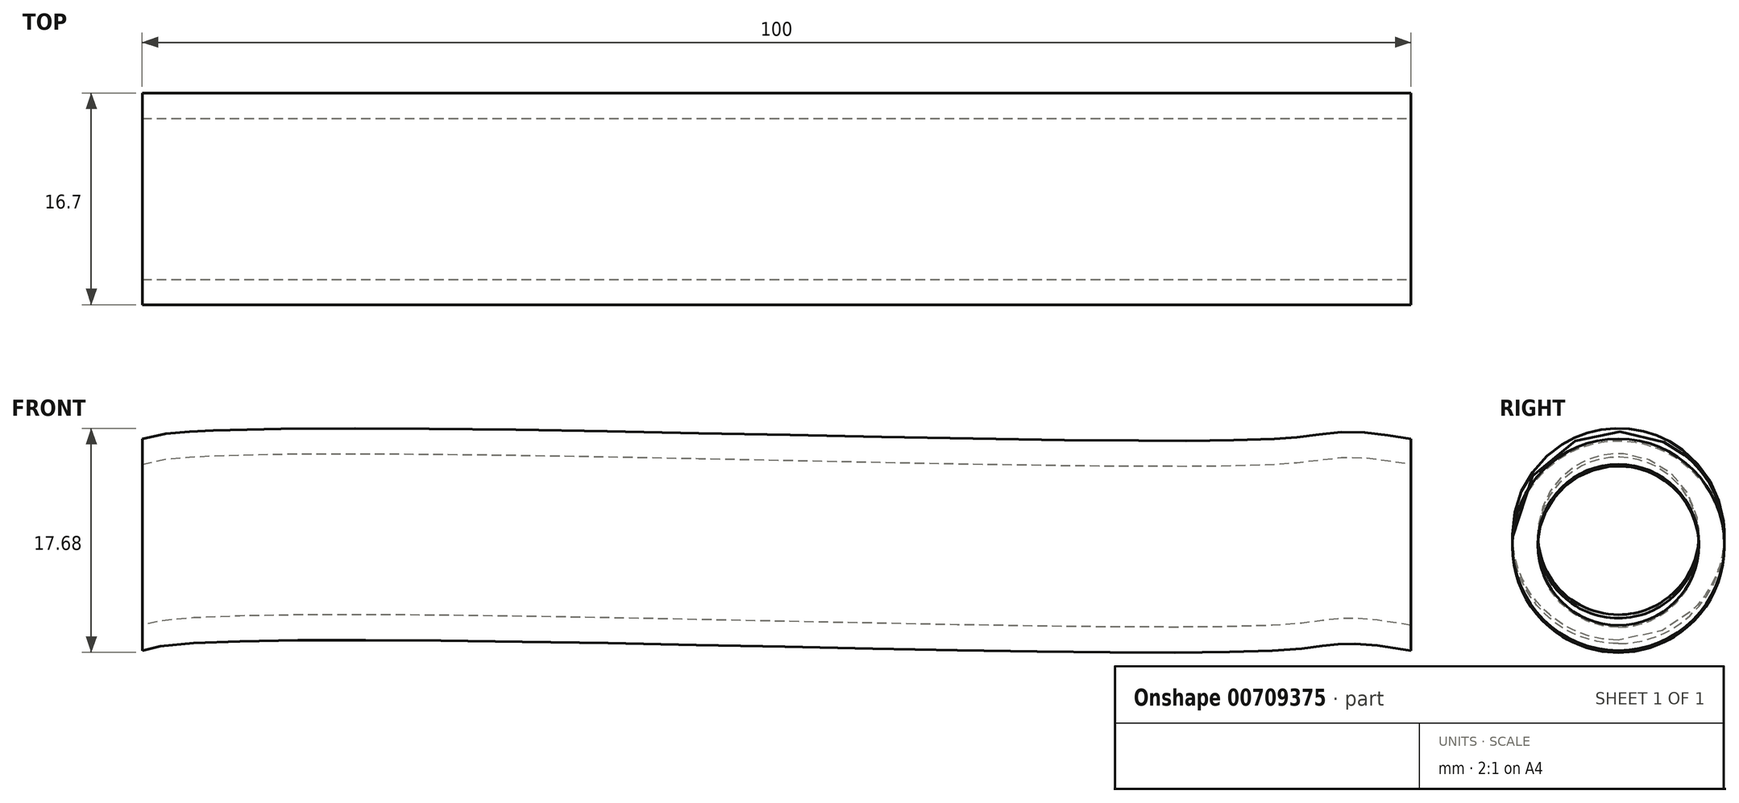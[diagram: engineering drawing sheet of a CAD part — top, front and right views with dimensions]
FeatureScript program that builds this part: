
annotation { "Feature Type Name" : "Feature", "Feature Type Description" : "" }
export const myFeature = defineFeature(function(context is Context, id is Id, definition is map)
    precondition{}
    {
        {
            var Q0;
            Q0=qCreatedBy(makeId("Front.planeOp"),FACE);
            var sketch = newSketch(context, id + "F0", { "sketchPlane" : qUnion([Q0])});
            skPoint(sketch, "E0", {"position": v(-19.42, 9.4) * mm});
            skPoint(sketch, "E1", {"position": v(80.58, 9.4) * mm});
            skFitSpline(sketch, "E2", {"points": [v(-19.42, 9.4) * mm, v(69.9, 9.4) * mm, v(80.58, 9.4) * mm], "startDerivative": vector(18.05, 9.02) * mm, "endDerivative": vector(73.66, -12.53) * mm});
            skSolve(sketch);
        }
        {
            var Q0;
            Q0=sQuery(id+"F0.wireOp",VERTEX,"E1");
            var Q1;
            Q1=qCreatedBy(makeId("Right.planeOp"),FACE);
            cPlane(context, id + "F1", {"entities" : qUnion([Q0, Q1]), "cplaneType" : CPlaneType.PLANE_POINT, "offset" : 25 * mm, "width" : 150 * mm, "height" : 150 * mm});
        }
        {
            var Q0;
            Q0=qCreatedBy(id+"F1.planeOp",FACE);
            var sketch = newSketch(context, id + "F2", { "sketchPlane" : qUnion([Q0])});
            skPoint(sketch, "E3.0", {"position": v(0, 9.4) * mm});
            skCircle(sketch, "E4", {"center": v(0, 9.4) * mm, "radius": 8.35 * mm});
            skCircle(sketch, "E5.0", {"center": v(0, 9.4) * mm, "radius": 6.35 * mm});
            skSolve(sketch);
        }
        {
            var Q0;
            Q0=makeQuery(id+"F2.imprint","IMPRINT",FACE,{"disambiguationData":[TD([[makeQuery(id+"F2.imprint","IMPRINT",EDGE,{"derivedFrom":sQuery(id+"F2.wireOp",EDGE,"E4")}),1.0]])]});
            var Q1;
            Q1=sQuery(id+"F0.wireOp",EDGE,"E2");
            sweep(context, id + "F3", {"profiles" : qUnion([Q0]), "path" : qUnion([Q1]), "keepProfileOrientation" : true});
        }
    });
